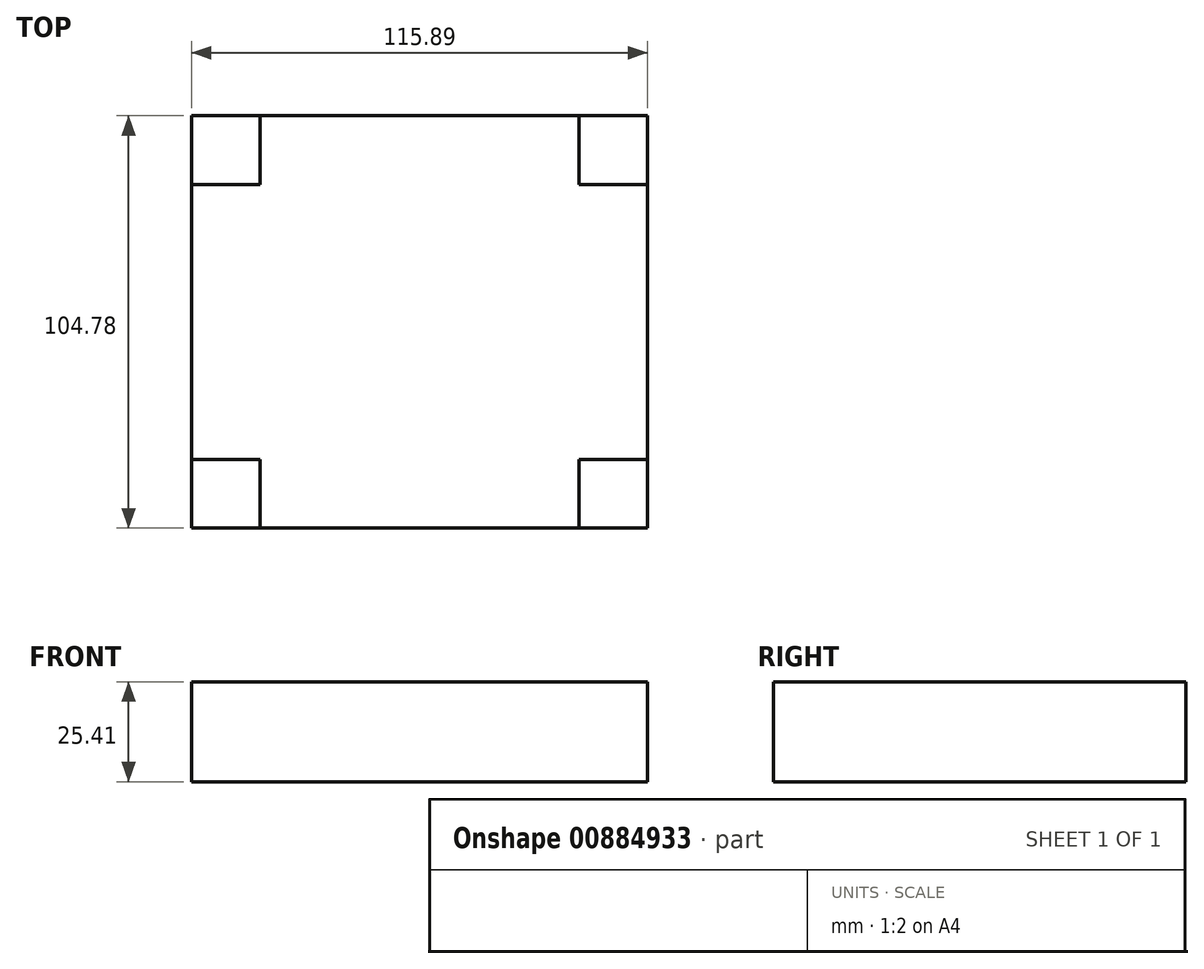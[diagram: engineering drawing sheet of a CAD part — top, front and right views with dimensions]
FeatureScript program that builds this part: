
annotation { "Feature Type Name" : "Feature", "Feature Type Description" : "" }
export const myFeature = defineFeature(function(context is Context, id is Id, definition is map)
    precondition{}
    {
        {
            var Q0;
            Q0=qCreatedBy(makeId("Top.planeOp"),FACE);
            var sketch = newSketch(context, id + "F0", { "sketchPlane" : qUnion([Q0])});
            skLineSegment(sketch, "E0.bottom", {"start": v(-57.5, 52) * mm, "end": v(58.39, 52) * mm});
            skLineSegment(sketch, "E0.top", {"start": v(-57.5, -52.78) * mm, "end": v(58.39, -52.78) * mm});
            skLineSegment(sketch, "E0.left", {"start": v(-57.5, 52) * mm, "end": v(-57.5, -52.78) * mm});
            skLineSegment(sketch, "E0.right", {"start": v(58.39, 52) * mm, "end": v(58.39, -52.78) * mm});
            skSolve(sketch);
        }
        {
            var Q0;
            Q0 = qSketchRegion(id + "F0", true);
            extrude(context, id + "F1", {"entities" : qUnion([Q0]), "depth" : 25.4 * mm + 1 / 101.6 * mm, "offsetDistance" : 25 * mm});
        }
        {
            var Q0;
            Q0=makeQuery(id+"F1.opExtrude","CAP_FACE",FACE,{"disambiguationData":[OSD([sQuery(id+"F0.wireOp",EDGE,"E0.bottom"),sQuery(id+"F0.wireOp",EDGE,"E0.top"),sQuery(id+"F0.wireOp",EDGE,"E0.left"),sQuery(id+"F0.wireOp",EDGE,"E0.right")])],"isStart":false});
            var sketch = newSketch(context, id + "F2", { "sketchPlane" : qUnion([Q0])});
            skLineSegment(sketch, "E1.bottom", {"start": v(-57.5, 52) * mm, "end": v(-40.04, 52) * mm});
            skLineSegment(sketch, "E1.top", {"start": v(-57.5, 34.54) * mm, "end": v(-40.04, 34.54) * mm});
            skLineSegment(sketch, "E1.left", {"start": v(-57.5, 52) * mm, "end": v(-57.5, 34.54) * mm});
            skLineSegment(sketch, "E1.right", {"start": v(-40.04, 52) * mm, "end": v(-40.04, 34.54) * mm});
            skPoint(sketch, "E2.endSnap0", {"position": v(0.44, 52) * mm});
            skPoint(sketch, "E3.startSnap0", {"position": v(-57.5, -0.39) * mm});
            skLineSegment(sketch, "E4.bottom", {"start": v(40.92, 52) * mm, "end": v(58.39, 52) * mm});
            skLineSegment(sketch, "E4.top", {"start": v(40.92, 34.54) * mm, "end": v(58.39, 34.54) * mm});
            skLineSegment(sketch, "E4.left", {"start": v(40.92, 52) * mm, "end": v(40.92, 34.54) * mm});
            skLineSegment(sketch, "E4.right", {"start": v(58.39, 52) * mm, "end": v(58.39, 34.54) * mm});
            skLineSegment(sketch, "E5.bottom", {"start": v(-57.5, -35.31) * mm, "end": v(-40.04, -35.31) * mm});
            skLineSegment(sketch, "E5.top", {"start": v(-57.5, -52.78) * mm, "end": v(-40.04, -52.78) * mm});
            skLineSegment(sketch, "E5.left", {"start": v(-57.5, -35.31) * mm, "end": v(-57.5, -52.78) * mm});
            skLineSegment(sketch, "E5.right", {"start": v(-40.04, -35.31) * mm, "end": v(-40.04, -52.78) * mm});
            skLineSegment(sketch, "E6.bottom", {"start": v(40.93, -52.78) * mm, "end": v(58.39, -52.78) * mm});
            skLineSegment(sketch, "E6.top", {"start": v(40.93, -35.31) * mm, "end": v(58.39, -35.31) * mm});
            skLineSegment(sketch, "E6.left", {"start": v(40.93, -52.78) * mm, "end": v(40.93, -35.31) * mm});
            skLineSegment(sketch, "E6.right", {"start": v(58.39, -52.78) * mm, "end": v(58.39, -35.31) * mm});
            skSolve(sketch);
        }
        {
            var Q0;
            Q0 = qSketchRegion(id + "F2", true);
            extrude(context, id + "F3", {"entities" : qUnion([Q0]), "operationType" : NewBodyOperationType.ADD, "depth" : 1 / 203.2 * mm, "offsetDistance" : 25 * mm});
        }
    });
